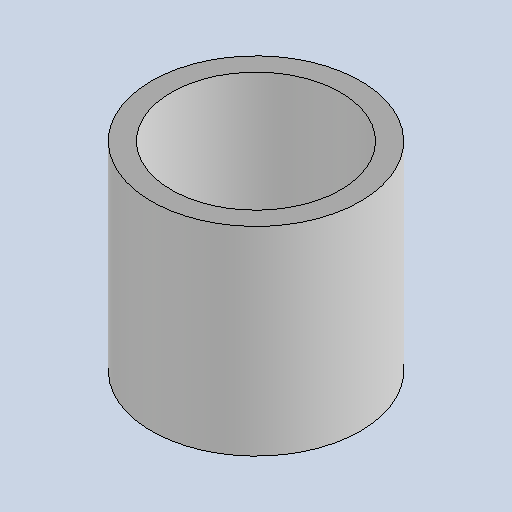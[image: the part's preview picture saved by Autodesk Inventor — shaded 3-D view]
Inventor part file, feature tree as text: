
AUTODESK INVENTOR PART (.ipt)
format: ipt  version: 2025.1 (Build 291241020, 241B)  size: 123,904 bytes
history: native  units: mm
features: extrude x1, sketch x1
ambient origin geometry x8: Origin, YZ Plane, XZ Plane, XY Plane, X Axis, Y Axis, Z Axis, Center Point
bodies: Body1 (feature_tree)
feature tree (2):
  extrude  "Extrusion5"  Depth=20.0mm
  sketch  "Sketch11"  dims[d187=21.0mm d188=2.0mm d189=20.0mm d190=0.0mm]
